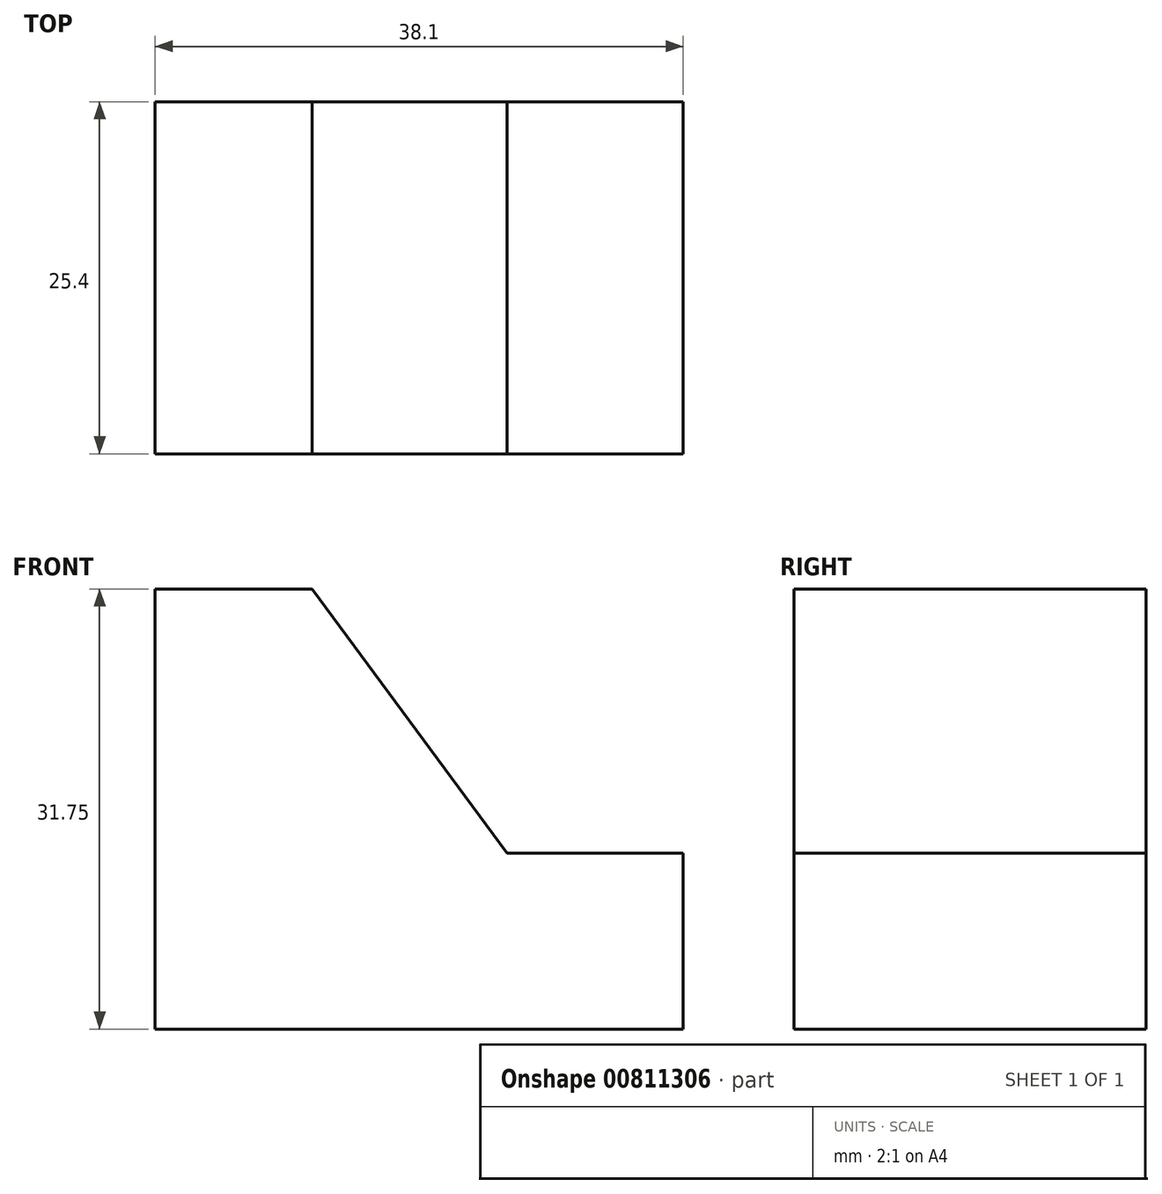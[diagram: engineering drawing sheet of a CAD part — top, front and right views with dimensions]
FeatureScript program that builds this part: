
annotation { "Feature Type Name" : "Feature", "Feature Type Description" : "" }
export const myFeature = defineFeature(function(context is Context, id is Id, definition is map)
    precondition{}
    {
        {
            var Q0;
            Q0=qCreatedBy(makeId("Front.planeOp"),FACE);
            var sketch = newSketch(context, id + "F0", { "sketchPlane" : qUnion([Q0])});
            skLineSegment(sketch, "E0", {"start": v(0, 0) * mm, "end": v(0, 31.75) * mm});
            skLineSegment(sketch, "E1", {"start": v(0, 31.75) * mm, "end": v(11.32, 31.75) * mm});
            skLineSegment(sketch, "E2", {"start": v(0, 0) * mm, "end": v(38.1, 0) * mm});
            skLineSegment(sketch, "E3", {"start": v(38.1, 0) * mm, "end": v(38.1, 12.7) * mm});
            skLineSegment(sketch, "E4", {"start": v(38.1, 12.7) * mm, "end": v(25.4, 12.7) * mm});
            skLineSegment(sketch, "E5", {"start": v(25.4, 12.7) * mm, "end": v(11.32, 31.75) * mm});
            skSolve(sketch);
        }
        {
            var Q0;
            Q0 = qSketchRegion(id + "F0", true);
            extrude(context, id + "F1", {"entities" : qUnion([Q0]), "depth" : 25.4 * mm, "offsetDistance" : 25.4 * mm});
        }
    });
